# Revit family: NLRS_57_DUF_UN_instortkanaal-instortpot-dubbel_LT_velu
name_source: partatom
category: Duct Fittings
units: mm (PartAtom-declared; Revit-internal decimal feet)

## family parameters
Always vertical = Yes
Cut with Voids When Loaded = No
Part Type = Tee
Round Connector Dimension = Use Diameter
Shared = No
Work Plane-Based = No

## types (6) — shared parameters
Assembly Code = 57.00
Description = Velu instort kanaal: Instortpot, dubbel
Manufacturer = Velu Klimaattechnische Groothandel
Model = VIK IPS dubbel
NLRS_C_content_datum_gewijzigd = 20-01-2023
NLRS_C_content_provider = Velu Klimaattechnische Groothandel
NLRS_C_content_versie = 3.20.01
NLRS_C_description = Velu instort kanaal: Instortpot, dubbel
Type Comments = Enkel geschikt voor VELU instort kanaal maten
URL = https://webshop.velu.nl
VELU_Article_Data = IPS_Dubbel
VELU_Model_Diameter = 78 mm  [stored 0.255906 ft]
VELU_Model_Diameter2 = 127 mm  [stored 0.416667 ft]
dummy = 1
zero-valued in all types: Default Elevation

## per-type parameters (varying)
| type | VELU_Koppelbus_Li2 |
| d=125, L=50 | 50 mm  [stored 0.164042 ft] |
| d=125, L=60 | 60 mm  [stored 0.19685 ft] |
| d=125, L=70 | 70 mm |
| d=125, L=80 | 80 mm  [stored 0.262467 ft] |
| d=125, L=90 | 90 mm  [stored 0.295276 ft] |
| d=125, L=100 | 100 mm  [stored 0.328084 ft] |

note: [stored X ft] marks values corroborated as IEEE doubles in the binary element streams (Revit-internal decimal feet)

## geometry (parser evidence)
native form markers: Sweep x5
no freeform markers — native parametric forms only
